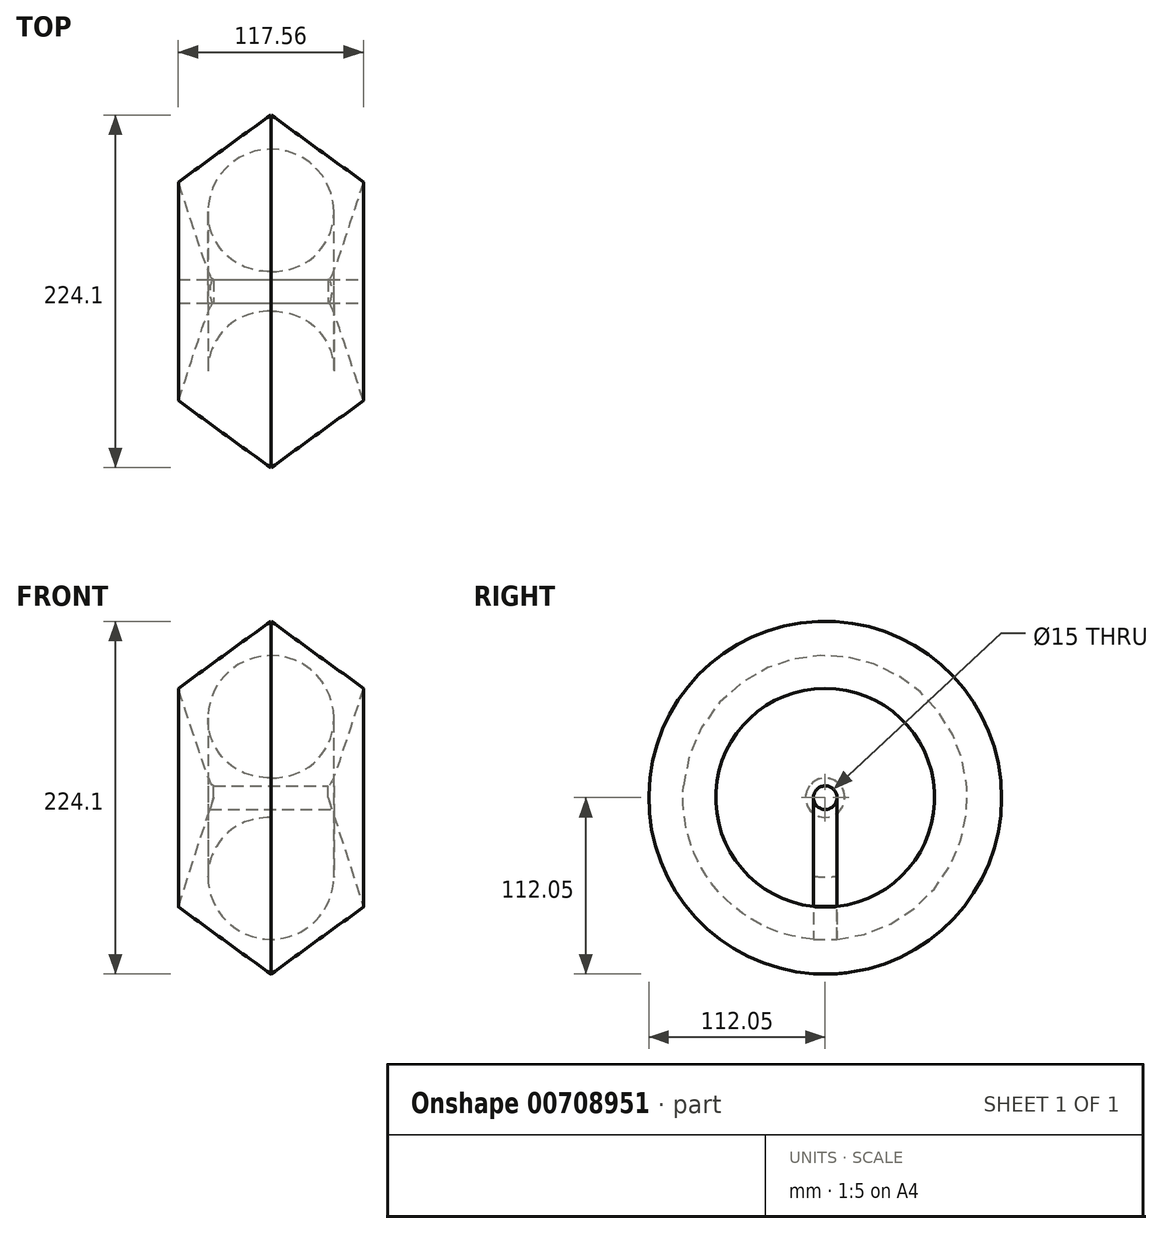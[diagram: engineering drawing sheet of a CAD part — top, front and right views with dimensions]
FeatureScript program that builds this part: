
annotation { "Feature Type Name" : "Feature", "Feature Type Description" : "" }
export const myFeature = defineFeature(function(context is Context, id is Id, definition is map)
    precondition{}
    {
        {
            var Q0;
            Q0=qCreatedBy(makeId("Front.planeOp"),FACE);
            var sketch = newSketch(context, id + "F0", { "sketchPlane" : qUnion([Q0])});
            skCircle(sketch, "E0.cCircle", {"center": v(0, 0) * mm, "radius": 50 * mm, "construction": true});
            skLineSegment(sketch, "E0.0", {"start": v(0, -61.8) * mm, "end": v(-58.78, -19.1) * mm});
            skLineSegment(sketch, "E0.1", {"start": v(-58.78, -19.1) * mm, "end": v(-36.33, 50) * mm});
            skLineSegment(sketch, "E0.2", {"start": v(-36.33, 50) * mm, "end": v(36.33, 50) * mm});
            skLineSegment(sketch, "E0.3", {"start": v(36.33, 50) * mm, "end": v(58.78, -19.1) * mm});
            skLineSegment(sketch, "E0.4", {"start": v(58.78, -19.1) * mm, "end": v(0, -61.8) * mm});
            skPoint(sketch, "E0.0.midPoint", {"position": v(-29.39, -40.45) * mm});
            skCircle(sketch, "E1", {"center": v(0, 0) * mm, "radius": 40 * mm});
            skSolve(sketch);
        }
        {
            var Q0;
            Q0 = qSketchRegion(id + "F0", true);
            extrude(context, id + "F1", {"entities" : qUnion([Q0]), "depth" : 15 * mm, "offsetDistance" : 25.4 * mm});
        }
        {
            var Q0;
            Q0=qCreatedBy(makeId("Right.planeOp"),FACE);
            var sketch = newSketch(context, id + "F2", { "sketchPlane" : qUnion([Q0])});
            skLineSegment(sketch, "E2.0", {"start": v(-15, -40) * mm, "end": v(-15, 40) * mm});
            skLineSegment(sketch, "E3.0", {"start": v(0, -40) * mm, "end": v(0, 40) * mm});
            skLineSegment(sketch, "E4", {"start": v(-15, 0) * mm, "end": v(0, 0) * mm});
            skLineSegment(sketch, "E5.0", {"start": v(-15, 50) * mm, "end": v(0, 50) * mm});
            skCircle(sketch, "E6", {"center": v(-7.5, 50) * mm, "radius": 50 * mm});
            skSolve(sketch);
        }
        {
            var Q0;
            Q0=makeQuery(id+"F1.opExtrude","CAP_FACE",FACE,{"disambiguationData":[OSD([sQuery(id+"F0.wireOp",EDGE,"E0.0"),sQuery(id+"F0.wireOp",EDGE,"E0.1"),sQuery(id+"F0.wireOp",EDGE,"E0.2"),sQuery(id+"F0.wireOp",EDGE,"E0.3"),sQuery(id+"F0.wireOp",EDGE,"E0.4"),sQuery(id+"F0.wireOp",EDGE,"E1")])],"isStart":false});
            var Q1;
            Q1=sQuery(id+"F2.wireOp",EDGE,"E6");
            sweep(context, id + "F3", {"operationType" : NewBodyOperationType.ADD, "profiles" : qUnion([Q0]), "path" : qUnion([Q1])});
        }
        {
            var Q0;
            Q0=qCreatedBy(makeId("Right.planeOp"),FACE);
            var sketch = newSketch(context, id + "F4", { "sketchPlane" : qUnion([Q0])});
            skArc(sketch, "E7.0", {"start": v(0, 50) * mm, "mid": v(-7.5, 57.5) * mm, "end": v(-15, 50) * mm});
            skCircle(sketch, "E8", {"center": v(-7.5, 50) * mm, "radius": 7.5 * mm});
            skSolve(sketch);
        }
        {
            var Q0;
            Q0 = qSketchRegion(id + "F4", true);
            extrude(context, id + "F5", {"entities" : qUnion([Q0]), "operationType" : NewBodyOperationType.REMOVE, "endBound" : BoundingType.SYMMETRIC, "oppositeDirection" : true, "depth" : 200 * mm, "offsetDistance" : 25.4 * mm});
        }
    });
